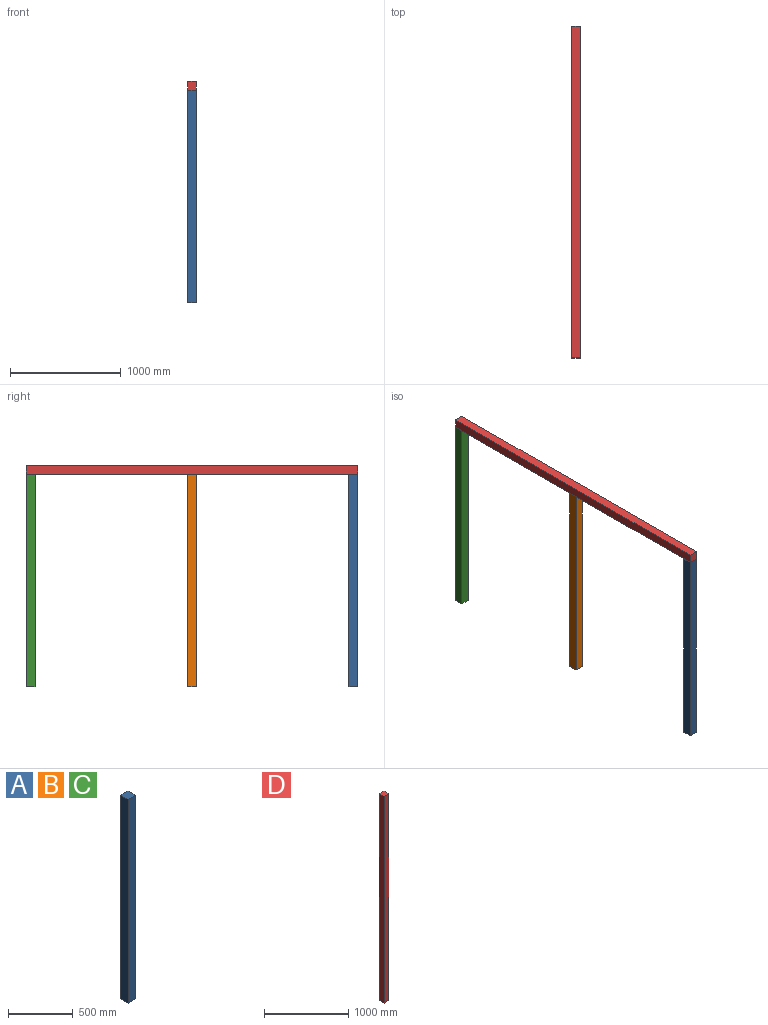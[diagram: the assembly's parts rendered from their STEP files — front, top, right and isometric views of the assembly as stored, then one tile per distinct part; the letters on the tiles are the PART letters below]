
ASSEMBLY  parts=4 mates=2
PART A: 6 faces, bbox 80x80x1920 mm
  f0: plane 1920x80mm, normal (0,1,0), area 153600mm2, adj f1,f3,f4,f5
  f1: plane 1920x80mm, normal (-1,0,0), area 153600mm2, adj f0,f2,f4,f5
  f2: plane 1920x80mm, normal (0,-1,0), area 153600mm2, adj f1,f3,f4,f5
  f3: plane 1920x80mm, normal (1,0,0), area 153600mm2, adj f0,f2,f4,f5
  f4: plane 80x80mm, normal (0,0,1), area 6400mm2, adj f0,f1,f2,f3
  f5: plane 80x80mm, normal (0,0,-1), area 6400mm2, adj f0,f1,f2,f3
PART B: same geometry as A
PART C: same geometry as A
PART D: 6 faces, bbox 80x80x3000 mm
  f0: plane 3000x80mm, normal (0,1,0), area 240000mm2, adj f1,f3,f4,f5
  f1: plane 3000x80mm, normal (-1,0,0), area 240000mm2, adj f0,f2,f4,f5
  f2: plane 3000x80mm, normal (0,-1,0), area 240000mm2, adj f1,f3,f4,f5
  f3: plane 3000x80mm, normal (1,0,0), area 240000mm2, adj f0,f2,f4,f5
  f4: plane 80x80mm, normal (0,0,1), area 6400mm2, adj f0,f1,f2,f3
  f5: plane 80x80mm, normal (0,0,-1), area 6400mm2, adj f0,f1,f2,f3
PLACE A t=(-440.85,-1437.78,-804.89)mm
PLACE B t=(-440.85,22.22,-804.89)mm
PLACE C t=(-440.85,1482.22,-804.89)mm
PLACE D rot(axis=(1,0,0),90deg) t=(-440.85,1522.22,1155.11)mm
MATE planar B.f4 <-> D.f2  axis (0,0,1) through (-440.85,22.22,1115.11)mm
MATE planar D.f2 <-> A.f4  axis (0,0,-1) through (-440.85,22.22,1115.11)mm
